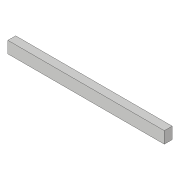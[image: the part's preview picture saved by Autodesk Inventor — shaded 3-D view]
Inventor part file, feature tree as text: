
AUTODESK INVENTOR PART (.ipt)
format: ipt  version: 2018 (Build 220112000, 112)  size: 75,264 bytes
history: native  units: in
note: dims shown in document units (in); Inventor stores cm internally (conversion verified against a paired STEP export)
features: extrude x1, sketch x1
ambient origin geometry x8: Origin, YZ Plane, XZ Plane, XY Plane, X Axis, Y Axis, Z Axis, Center Point
bodies: Solid1 (feature_tree)
feature tree (2):
  extrude  "Extrusion1"  TaperAngle=90.0deg  [1 undecoded]
  sketch  "Sketch1"  dims[d0=0.2953in d1=90.0deg d2=3.937in d3=90.0deg d4=0.2953in d5=90.0deg d6=0.1969in d7=0.0in]
note: 1 required parameter value undecoded (feature->parameter linkage not recoverable at this tier; creation-order binding heuristic only, values carry confidence <= 0.55)
